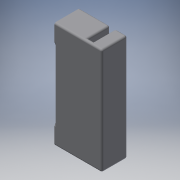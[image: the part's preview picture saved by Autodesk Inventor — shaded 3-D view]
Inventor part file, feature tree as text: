
AUTODESK INVENTOR PART (.ipt)
format: ipt  version: 2018 (Build 220112000, 112)  size: 438,784 bytes
history: native  units: in
note: dims shown in document units (in); Inventor stores cm internally (conversion verified against a paired STEP export)
features: reference x20, extrude x12, sketch x12, other x10, fillet x8, projected_geometry x4, plane x3
ambient origin geometry x8: Origin, YZ Plane, XZ Plane, XY Plane, X Axis, Y Axis, Z Axis, Center Point
bodies: Solid1 (feature_tree)
feature tree (69):
  extrude  "Extrusion1"  Depth=0.125in
  extrude  "Extrusion2"  Depth=0.4724in TaperAngle=0.0deg
  extrude  "Extrusion3"  Depth=0.2in TaperAngle=0.0deg
  extrude  "Extrusion4"  Depth=0.4in
  extrude  "Extrusion5"  Depth=0.25in
  extrude  "Extrusion6"  Depth=0.0787in TaperAngle=0.0deg
  fillet  "Fillet1"  Radius=0.125in
  fillet  "Fillet4"  Radius=0.1181in
  sketch  "Sketch8"  dims[d19=0.125in d20=0.1181in]
  plane  "Work Plane1"
  extrude  "Extrusion7"  Depth=0.1181in
  sketch  "Sketch9"  dims[d21=1.15in d22=0.0787in d23=0.0in d24=0.0394in d27=0.0394in d28=0.0197in d29=0.0197in]
  plane  "Work Plane2"
  extrude  "Extrusion8"  Depth=0.0394in TaperAngle=0.0deg
  fillet  "Fillet5"  Radius=0.0394in
  fillet  "Fillet6"  Radius=0.0394in
  fillet  "Fillet7"  Radius=0.0197in
  fillet  "Fillet9"  Radius=0.0197in
  sketch  "Sketch10"  dims[d30=1.0in d31=0.0in d32=0.0394in d33=0.0394in d34=1.0in d35=0.0in]
  plane  "Work Plane3"
  extrude  "Extrusion9"  Depth=0.0394in
  fillet  "Fillet10"  Radius=0.0394in
  fillet  "Fillet11"  Radius=1.0in
  extrude  "Extrusion10"  Depth=0.0394in
  extrude  "Extrusion11"  Depth=0.0394in
  extrude  "Extrusion12"  Depth=0.2362in TaperAngle=0.0deg
  sketch  "Sketch1"  dims[d0=0.5in d1=0.125in]
  reference  "Reference1"
  reference  "Reference2"
  reference  "Reference3"
  reference  "Reference4"
  reference  "Reference5"
  reference  "Reference6"
  reference  "Reference7"
  reference  "Reference8"
  reference  "Reference9"
  reference  "Reference10"
  reference  "Reference11"
  reference  "Reference12"
  reference  "Reference13"
  reference  "Reference14"
  reference  "Reference15"
  reference  "Reference16"
  reference  "Reference17"
  sketch  "Sketch2"  dims[d2=0.7in d3=0.4724in d4=0.0in]
  projected_geometry  "Projected Loop1"
  projected_geometry  "Projected Loop2"
  sketch  "Sketch4"  dims[d5=0.0787in d6=0.0in d7=0.2in d8=0.0in]
  projected_geometry  "Projected Loop3"
  sketch  "Sketch5"  dims[d9=0.4in d10=0.4in]
  reference  "Reference20"
  sketch  "Sketch6"  dims[d11=0.5512in d12=0.0in d13=0.25in]
  sketch  "Sketch7"  dims[d14=0.25in d15=0.0787in d16=0.0in d17=0.125in d18=0.1181in]
  projected_geometry  "Projected Loop4"
  sketch  "Sketch11"  dims[d36=0.0394in d37=0.0394in]
  sketch  "Sketch12"  dims[d38=0.0394in d40=0.0394in]
  sketch  "Sketch13"  dims[d41=0.0098in d42=1.0in d43=0.0in d44=0.0394in d45=0.0394in d46=12.0in d47=0.0in d48=0.0984in d49=0.0984in d50=0.315in d51=0.0in d52=0.0984in d53=0.0984in d54=0.2362in d55=0.0in]
  reference  "Reference21"
  reference  "Reference22"
  other  "<userpath>\OneDrive\Documents\Inventor\TSA\2018\Animatronics\Tortoise\TurtleAssembly.iam"
  other  "TurtleAssembly.iam"
  other  "servo (2):1"
  other  "smallergear:4"
  other  "<userpath>\OneDrive\Documents\Inventor\TSA\2018\Animatronics\Tortoise\AssemblyTURTLE.iam"
  other  "AssemblyTURTLE.iam"
  other  "Frame:1"
  other  "FronWheelDriveAssembly.iam"
  other  "steer_servo_mount2:2"
  other  "steer_servo_mount2:1"
